# Revit family: 72687117 iCONstant T - BIM file
name_source: partatom
category: Mechanical Equipment
units: mm (PartAtom-declared; Revit-internal decimal feet)

## family parameters
Cut with Voids When Loaded = No
Host = Face
Maintain Annotation Orientation = No
Part Type = Normal
Room Calculation Point = No
Round Connector Dimension = Use Diameter
Shared = No

## types (2) — shared parameters
6MonthlyMaintenance = Visually inspect system, clean the fan and ducting if necessary
A = 197 mm
AccessClearanceBottom = 350 mm
AccessClearanceFront = 350 mm
AccessClearanceLeft = 350 mm
AccessClearanceRight = 350 mm
AccessClearanceTop = 350 mm
AssemblyPlace = UKNOWN
AssetType = Fixed
BMSLinks = No
C = 70 mm
CEApproval = Yes
CapacityControlType = Variable Speed Drive
Category = Pr_65_67_29_05:Axial Flow Fans
Color = White
D = 100 mm  [stored 0.328084 ft]
Default Elevation = 1219 mm
Description = The quietest continuous extract (dMEV) fan available on the market
DesignOfDomesticVentilation = This fan should provide the minimum flow rates outlined and installed in line with Approved Document Part F of the Building Regulations.
Ductwork = 100mm flexible or rigid
DurationUnit = Year
E = 50 mm  [stored 0.164042 ft]
ErPEnergyRating = C
Exclusions = Hasn't been installed or used in accordance with the instructions
Connected with an unsuitable electrical supply
Has been misused, neglected or damaged
Modified or repaired by someone not authorised by Airflow Developments Ltd
Hasn't been installed according to Building Regulations or IEEE wiring regulations
ExpectedServiceLife = 3
Export Type to IFC As = IfcFanType
ExternalExhaustAirTerminals = 90% free air grille
Fan = Domestic continuously running (dMEV) axial fan
Features = Extracts up to 20l/sec
Noise levels just 10dB(A)
IPX5 Rated
SAP Appendix Q eligible
Guarantee constant pressure and constant volume feature
Finish = Matte
FireControlPanelLinks = No
Grade = Virgin
GrossWeight = 0.55 kg
HasPartWinding = Yes
HasProtectiveEarth = No
IP_Code = IPX5
ISO140001 = Yes
ISO90001 = Yes
IfcExportAs = IfcFanType
IfcExportType = NOTDEFINED
InsulationStandardClass = Double Insulated
IsExtendedWarranty = No
IsGuarded = Yes
Manufacturer = Airflow Developments Ltd
ManufacturerAddress = Aidelle House
Lancaster Road
Cressex Business Park
High Wycombe
Bucks
HP123QP
ManufacturerTelephone = 01494 525252
ManufacturerWebsite = www.airflow.com
Material = Plastic
MotorDriveType = Direct Drive
MotorEnclosureType = Totally Enclosed Air Over
NBSCode = 90-45-30/310 Axial flow fans;
NominalFrequencyRange = 60
NominalHeight = 197 mm
NominalLength = 120 mm
NominalPowerRate = 3 W
NominalRotationSpeed = 69 Hz
NominalStaticPressure = 23.0 Pa
NominalWidth = 197 mm
NumberOfPoles = 1
OperationTemperatureRange = up to 40°C
PointOfContact = Airflow Developments Ltd
PowerSource = System-powered
ProductionYear = 2017
QuietMarkApproval = No
RatedCurrent = 3 A
RatedVoltage = 110 V
RedDotDesignAward = No
RoomExtractAirTerminalDevices = Continuous extract fan (dMEV) for residential properties
ServiceLifeDuration = 3
ServiceLifeType = ExpectedServiceLife
Shape = Round
ShippingWeight = 0.75 kg
Size = 120 x 197 x 197
StartingTime = 5.0 s
Status = New
SupplyPhase = 1
Type IFC Predefined Type = NOTDEFINED
Uniclass2015 = Pr_65_67_29_05
WarrantyContent = Covered against faulty material or workmanship - not reinstallation if needed
WarrantyGuarantor = Airflow Developments Ltd
WarrantyPeriod = 2
WarrantyPeriodForMotors = 1
WarrantyPeriodWhenRegistered = 3
iCONstant = CADS_AirFlow_White
zero-valued in all types: AccessClearanceRear

## per-type parameters (varying)
| type | Controls | GlobalTradeItemNumber | Humidity_Timer | ModelLabel | ModelReference | NominalAirFlowRate | Quantity | ReplacementCost | Timer |
| ICSTT | Timer. On boost timer run on for 2, 15, 30 or 40mins | 5019009318288 | No | iCONstant T | 72687117 | 20.0 L/s | 0 | 191.736 | Yes |
| ICSTHT | Humidity Timer. Adjustable humidity sensor (60-90% relative humidity). On boost timer run on for 2, 15,30 or 40mins | 5019009318295 | Yes | iCONstant HT | 72687118 | 22.0 L/s | 1 | 232.92 | No |

note: column(s) folded — value = type name in every type: Type

note: [stored X ft] marks values corroborated as IEEE doubles in the binary element streams (Revit-internal decimal feet)

## geometry (parser evidence)
native form markers: Blend x12, Sweep x4
no freeform markers — native parametric forms only
